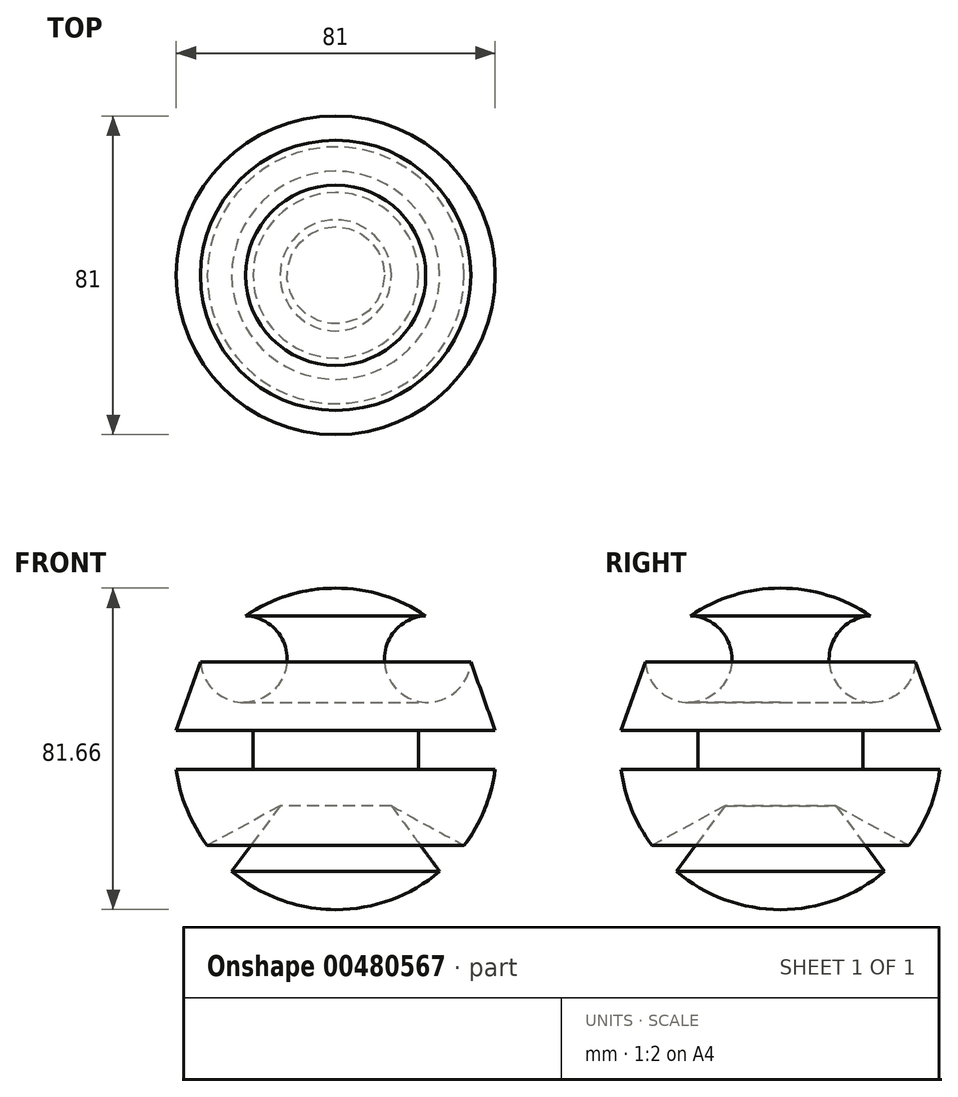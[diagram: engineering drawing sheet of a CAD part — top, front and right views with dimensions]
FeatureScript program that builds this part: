
annotation { "Feature Type Name" : "Feature", "Feature Type Description" : "" }
export const myFeature = defineFeature(function(context is Context, id is Id, definition is map)
    precondition{}
    {
        {
            var Q0;
            Q0=qCreatedBy(makeId("Front.planeOp"),FACE);
            var sketch = newSketch(context, id + "F0", { "sketchPlane" : qUnion([Q0])});
            skArc(sketch, "E0", {"start": v(-40.5, -5.25) * mm, "mid": v(-37.82, -15.4) * mm, "end": v(-32.64, -24.54) * mm});
            skArc(sketch, "E1", {"start": v(-34.33, 22.11) * mm, "mid": v(-15.5, 15.15) * mm, "end": v(-22.88, 33.83) * mm});
            skLineSegment(sketch, "E2", {"start": v(-32.64, -24.54) * mm, "end": v(-14.12, -14.48) * mm});
            skLineSegment(sketch, "E3", {"start": v(-14.12, -14.48) * mm, "end": v(-26.43, -31.13) * mm});
            skArc(sketch, "E4.trimOffspring", {"start": v(-26.43, -31.13) * mm, "mid": v(40.77, -2.23) * mm, "end": v(-22.88, 33.83) * mm});
            skLineSegment(sketch, "E5", {"start": v(0, 40.83) * mm, "end": v(0, -40.83) * mm});
            skLineSegment(sketch, "E6.bottom", {"start": v(-21, 4.7) * mm, "end": v(-40.5, 4.7) * mm});
            skLineSegment(sketch, "E6.top", {"start": v(-21, -5.25) * mm, "end": v(-40.5, -5.25) * mm});
            skLineSegment(sketch, "E6.left", {"start": v(-21, 4.7) * mm, "end": v(-21, -5.25) * mm});
            skLineSegment(sketch, "E7", {"start": v(-40.5, 4.7) * mm, "end": v(-34.33, 22.11) * mm});
            skSolve(sketch);
        }
        {
            var Q0;
            Q0=makeQuery(id+"F0.imprint","IMPRINT",FACE,{"disambiguationData":[TD([[makeQuery(id+"F0.imprint","IMPRINT",EDGE,{"derivedFrom":sQuery(id+"F0.wireOp",EDGE,"E0")}),1.0]])]});
            var Q1;
            Q1=sQuery(id+"F0.wireOp",EDGE,"E5");
            revolve(context, id + "F1", {"entities" : qUnion([Q0]), "axis" : qUnion([Q1]), "revolveType" : RevolveType.FULL});
        }
    });
